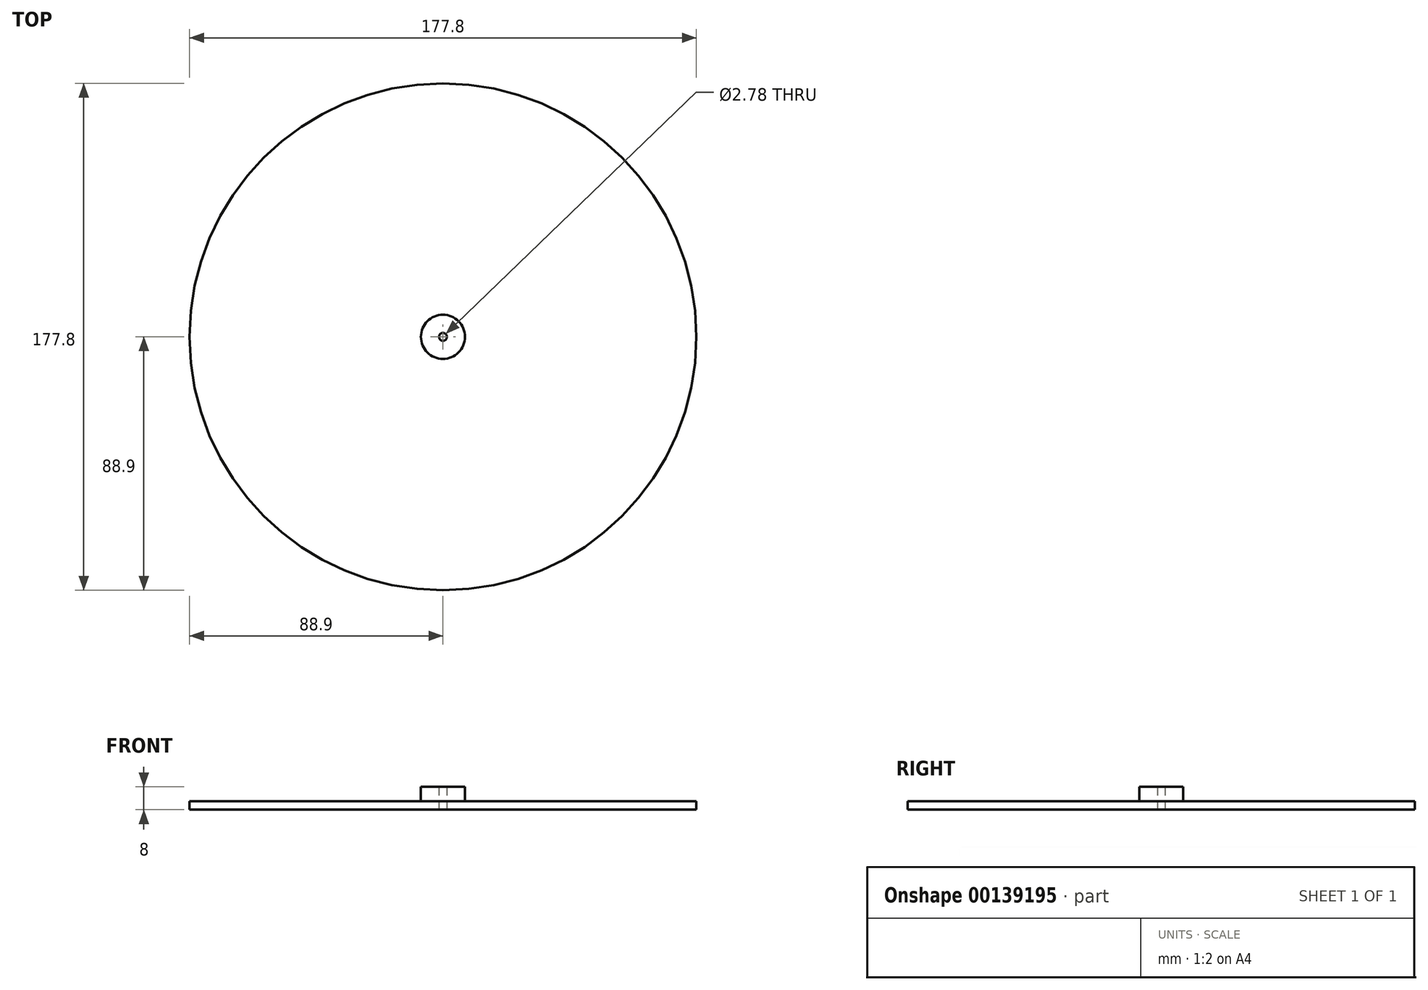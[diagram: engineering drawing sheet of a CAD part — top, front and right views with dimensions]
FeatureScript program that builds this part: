
annotation { "Feature Type Name" : "Feature", "Feature Type Description" : "" }
export const myFeature = defineFeature(function(context is Context, id is Id, definition is map)
    precondition{}
    {
        {
            var Q0;
            Q0=qCreatedBy(makeId("Front.planeOp"),FACE);
            var sketch = newSketch(context, id + "F0", { "sketchPlane" : qUnion([Q0])});
            skLineSegment(sketch, "E0", {"start": v(0, 0) * mm, "end": v(0, 14.25) * mm});
            skLineSegment(sketch, "E1.bottom", {"start": v(1.39, -1.72) * mm, "end": v(7.74, -1.72) * mm});
            skLineSegment(sketch, "E1.top", {"start": v(1.39, 6.28) * mm, "end": v(7.74, 6.28) * mm});
            skLineSegment(sketch, "E1.left", {"start": v(1.39, -1.72) * mm, "end": v(1.39, 6.28) * mm});
            skLineSegment(sketch, "E1.right", {"start": v(7.74, 1.28) * mm, "end": v(7.74, 6.28) * mm});
            skLineSegment(sketch, "E2.bottom", {"start": v(7.74, -1.72) * mm, "end": v(88.9, -1.72) * mm});
            skLineSegment(sketch, "E2.top", {"start": v(7.74, 1.28) * mm, "end": v(88.9, 1.28) * mm});
            skLineSegment(sketch, "E2.right", {"start": v(88.9, -1.72) * mm, "end": v(88.9, 1.28) * mm});
            skSolve(sketch);
        }
        {
            var Q0;
            Q0=makeQuery(id+"F0.imprint","IMPRINT",FACE,{"disambiguationData":[TD([[makeQuery(id+"F0.imprint","IMPRINT",EDGE,{"derivedFrom":sQuery(id+"F0.wireOp",EDGE,"E1.bottom")}),1.0]])]});
            var Q1;
            Q1=sQuery(id+"F0.wireOp",EDGE,"E0");
            revolve(context, id + "F1", {"entities" : qUnion([Q0]), "axis" : qUnion([Q1]), "revolveType" : RevolveType.FULL});
        }
    });
